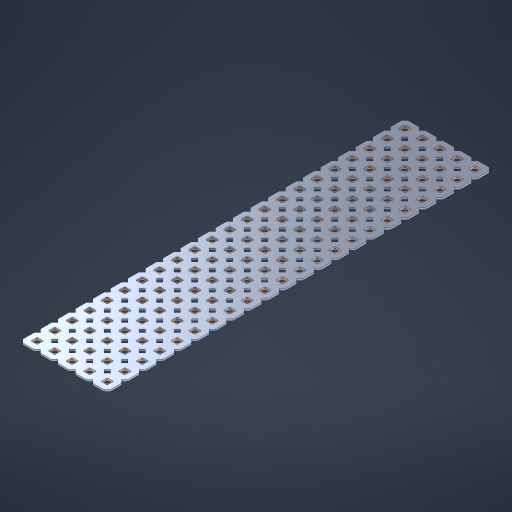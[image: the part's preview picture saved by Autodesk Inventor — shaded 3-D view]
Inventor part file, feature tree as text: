
AUTODESK INVENTOR PART (.ipt)
format: ipt  version: 2023 (Build 270158000, 158)  size: 1,531,392 bytes
history: native  units: in
note: dims shown in document units (in); Inventor stores cm internally (conversion verified against a paired STEP export)
features: other x111, extrude x109, sketch x2, pattern_linear x1
ambient origin geometry x8: Origin, YZ Plane, XZ Plane, XY Plane, X Axis, Y Axis, Z Axis, Center Point
bodies: Solid1 (feature_tree), Body (feature_tree)
feature tree (223):
  pattern_linear  "Rectangular Pattern1"  Spacing1=0.09in  [1 undecoded]
  sketch  "Sketch1"  dims[d1=0.5in]
  sketch  "Sketch2"  dims[d2=0.182in d3=0.09in d4=0.09in d5=0.09in d6=0.09in d7=0.09in d8=0.09in d9=0.09in d10=0.09in d11=0.02in d13=0.0in d14=0.172in d15=0.0625in d16=0.0in d19=0.5in d22=0.5in]
  other  "Srf1"
  other  "Srf126"
  other  "Srf127"
  other  "Srf128"
  other  "Srf129"
  other  "Srf130"
  other  "Srf131"
  other  "Srf250"
  other  "Srf251"
  other  "Srf252"
  other  "Srf253"
  other  "Srf254"
  other  "Srf255"
  other  "Srf256"
  other  "Srf257"
  other  "Srf258"
  other  "Srf259"
  other  "Srf260"
  other  "Srf261"
  other  "Srf262"
  other  "Srf263"
  other  "Srf264"
  other  "Srf268"
  other  "Srf269"
  other  "Srf270"
  other  "Srf271"
  other  "Srf272"
  other  "Srf273"
  other  "Srf274"
  other  "Srf275"
  other  "Srf276"
  other  "Srf277"
  other  "Srf278"
  other  "Srf279"
  other  "Srf280"
  other  "Srf281"
  other  "Srf282"
  other  "Srf283"
  other  "Srf284"
  other  "Srf285"
  other  "Srf286"
  other  "Srf287"
  other  "Srf288"
  other  "Srf289"
  other  "Srf293"
  other  "Srf294"
  other  "Srf295"
  other  "Srf296"
  other  "Srf297"
  other  "Srf298"
  other  "Srf299"
  other  "Srf300"
  other  "Srf301"
  other  "Srf302"
  other  "Srf303"
  other  "Srf304"
  other  "Srf305"
  other  "Srf306"
  other  "Srf307"
  other  "Srf308"
  other  "Srf309"
  other  "Srf310"
  other  "Srf311"
  other  "Srf312"
  other  "Srf313"
  other  "Srf314"
  other  "Srf318"
  other  "Srf319"
  other  "Srf320"
  other  "Srf321"
  other  "Srf322"
  other  "Srf323"
  other  "Srf324"
  other  "Srf325"
  other  "Srf326"
  other  "Srf327"
  other  "Srf328"
  other  "Srf329"
  other  "Srf330"
  other  "Srf331"
  other  "Srf332"
  other  "Srf333"
  other  "Srf334"
  other  "Srf335"
  other  "Srf336"
  other  "Srf337"
  other  "Srf338"
  other  "Srf339"
  other  "Srf343"
  other  "Srf344"
  other  "Srf345"
  other  "Srf346"
  other  "Srf347"
  other  "Srf348"
  other  "Srf349"
  other  "Srf350"
  other  "Srf351"
  other  "Srf352"
  other  "Srf353"
  other  "Srf354"
  other  "Srf355"
  other  "Srf356"
  other  "Srf357"
  other  "Srf358"
  other  "Srf359"
  other  "Srf360"
  other  "Srf361"
  other  "Srf362"
  other  "Srf363"
  other  "Srf364"
  other  "Circle"
  extrude  "ExtrusionSrf126"  Depth=0.09in
  extrude  "ExtrusionSrf127"  Depth=0.09in
  extrude  "ExtrusionSrf128"  Depth=0.09in
  extrude  "ExtrusionSrf129"  Depth=0.09in
  extrude  "ExtrusionSrf130"  Depth=0.09in
  extrude  "ExtrusionSrf131"  Depth=0.09in
  extrude  "ExtrusionSrf250"  Depth=0.09in
  extrude  "ExtrusionSrf251"  Depth=0.02in
  extrude  "ExtrusionSrf252"  TaperAngle=0.0deg  [1 undecoded]
  extrude  "ExtrusionSrf253"  Depth=0.5in
  extrude  "ExtrusionSrf254"  Depth=0.5in TaperAngle=0.0deg
  extrude  "ExtrusionSrf255"  Depth=0.5in
  extrude  "ExtrusionSrf256"  Depth=0.5in
  extrude  "ExtrusionSrf257"  [1 undecoded]
  extrude  "ExtrusionSrf258"  [1 undecoded]
  extrude  "ExtrusionSrf259"  [1 undecoded]
  extrude  "ExtrusionSrf260"  [1 undecoded]
  extrude  "ExtrusionSrf261"  [1 undecoded]
  extrude  "ExtrusionSrf262"  [1 undecoded]
  extrude  "ExtrusionSrf263"  [1 undecoded]
  extrude  "ExtrusionSrf264"  [1 undecoded]
  extrude  "ExtrusionSrf268"  [1 undecoded]
  extrude  "ExtrusionSrf269"  [1 undecoded]
  extrude  "ExtrusionSrf270"  [1 undecoded]
  extrude  "ExtrusionSrf271"  [1 undecoded]
  extrude  "ExtrusionSrf272"  [1 undecoded]
  extrude  "ExtrusionSrf273"  [1 undecoded]
  extrude  "ExtrusionSrf274"  [1 undecoded]
  extrude  "ExtrusionSrf275"  [1 undecoded]
  extrude  "ExtrusionSrf276"  [1 undecoded]
  extrude  "ExtrusionSrf277"  [1 undecoded]
  extrude  "ExtrusionSrf278"  [1 undecoded]
  extrude  "ExtrusionSrf279"  [1 undecoded]
  extrude  "ExtrusionSrf280"  [1 undecoded]
  extrude  "ExtrusionSrf281"  [1 undecoded]
  extrude  "ExtrusionSrf282"  [1 undecoded]
  extrude  "ExtrusionSrf283"  [1 undecoded]
  extrude  "ExtrusionSrf284"  [1 undecoded]
  extrude  "ExtrusionSrf285"  [1 undecoded]
  extrude  "ExtrusionSrf286"  [1 undecoded]
  extrude  "ExtrusionSrf287"  [1 undecoded]
  extrude  "ExtrusionSrf288"  [1 undecoded]
  extrude  "ExtrusionSrf289"  [1 undecoded]
  extrude  "ExtrusionSrf293"  [1 undecoded]
  extrude  "ExtrusionSrf294"  [1 undecoded]
  extrude  "ExtrusionSrf295"  [1 undecoded]
  extrude  "ExtrusionSrf296"  [1 undecoded]
  extrude  "ExtrusionSrf297"  [1 undecoded]
  extrude  "ExtrusionSrf298"  [1 undecoded]
  extrude  "ExtrusionSrf299"  [1 undecoded]
  extrude  "ExtrusionSrf300"  [1 undecoded]
  extrude  "ExtrusionSrf301"  [1 undecoded]
  extrude  "ExtrusionSrf302"  [1 undecoded]
  extrude  "ExtrusionSrf303"  [1 undecoded]
  extrude  "ExtrusionSrf304"  [1 undecoded]
  extrude  "ExtrusionSrf305"  [1 undecoded]
  extrude  "ExtrusionSrf306"  [1 undecoded]
  extrude  "ExtrusionSrf307"  [1 undecoded]
  extrude  "ExtrusionSrf308"  [1 undecoded]
  extrude  "ExtrusionSrf309"  [1 undecoded]
  extrude  "ExtrusionSrf310"  [1 undecoded]
  extrude  "ExtrusionSrf311"  [1 undecoded]
  extrude  "ExtrusionSrf312"  [1 undecoded]
  extrude  "ExtrusionSrf313"  [1 undecoded]
  extrude  "ExtrusionSrf314"  [1 undecoded]
  extrude  "ExtrusionSrf318"  [1 undecoded]
  extrude  "ExtrusionSrf319"  [1 undecoded]
  extrude  "ExtrusionSrf320"  [1 undecoded]
  extrude  "ExtrusionSrf321"  [1 undecoded]
  extrude  "ExtrusionSrf322"  [1 undecoded]
  extrude  "ExtrusionSrf323"  [1 undecoded]
  extrude  "ExtrusionSrf324"  [1 undecoded]
  extrude  "ExtrusionSrf325"  [1 undecoded]
  extrude  "ExtrusionSrf326"  [1 undecoded]
  extrude  "ExtrusionSrf327"  [1 undecoded]
  extrude  "ExtrusionSrf328"  [1 undecoded]
  extrude  "ExtrusionSrf329"  [1 undecoded]
  extrude  "ExtrusionSrf330"  [1 undecoded]
  extrude  "ExtrusionSrf331"  [1 undecoded]
  extrude  "ExtrusionSrf332"  [1 undecoded]
  extrude  "ExtrusionSrf333"  [1 undecoded]
  extrude  "ExtrusionSrf334"  [1 undecoded]
  extrude  "ExtrusionSrf335"  [1 undecoded]
  extrude  "ExtrusionSrf336"  [1 undecoded]
  extrude  "ExtrusionSrf337"  [1 undecoded]
  extrude  "ExtrusionSrf338"  [1 undecoded]
  extrude  "ExtrusionSrf339"  [1 undecoded]
  extrude  "ExtrusionSrf343"  [1 undecoded]
  extrude  "ExtrusionSrf344"  [1 undecoded]
  extrude  "ExtrusionSrf345"  [1 undecoded]
  extrude  "ExtrusionSrf346"  [1 undecoded]
  extrude  "ExtrusionSrf347"  [1 undecoded]
  extrude  "ExtrusionSrf348"  [1 undecoded]
  extrude  "ExtrusionSrf349"  [1 undecoded]
  extrude  "ExtrusionSrf350"  [1 undecoded]
  extrude  "ExtrusionSrf351"  [1 undecoded]
  extrude  "ExtrusionSrf352"  [1 undecoded]
  extrude  "ExtrusionSrf353"  [1 undecoded]
  extrude  "ExtrusionSrf354"  [1 undecoded]
  extrude  "ExtrusionSrf355"  [1 undecoded]
  extrude  "ExtrusionSrf356"  [1 undecoded]
  extrude  "ExtrusionSrf357"  [1 undecoded]
  extrude  "ExtrusionSrf358"  [1 undecoded]
  extrude  "ExtrusionSrf359"  [1 undecoded]
  extrude  "ExtrusionSrf360"  [1 undecoded]
  extrude  "ExtrusionSrf361"  [1 undecoded]
  extrude  "ExtrusionSrf362"  [1 undecoded]
  extrude  "ExtrusionSrf363"  [1 undecoded]
  extrude  "ExtrusionSrf364"  [1 undecoded]
note: 98 required parameter values undecoded (feature->parameter linkage not recoverable at this tier; creation-order binding heuristic only, values carry confidence <= 0.55)
